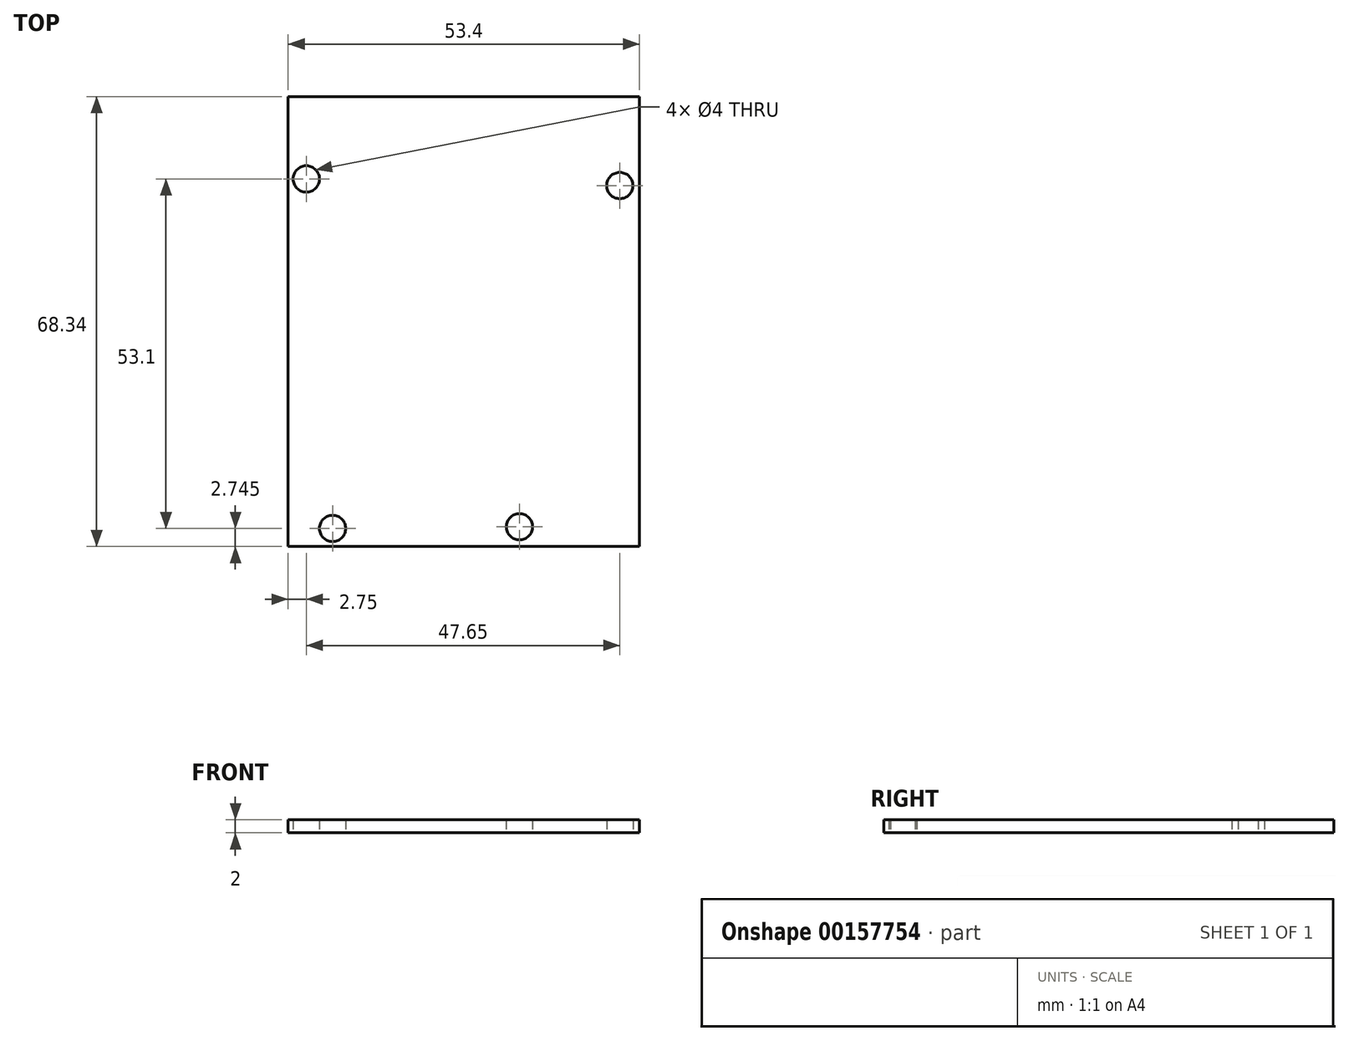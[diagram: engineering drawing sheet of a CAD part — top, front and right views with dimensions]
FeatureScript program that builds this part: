
annotation { "Feature Type Name" : "Feature", "Feature Type Description" : "" }
export const myFeature = defineFeature(function(context is Context, id is Id, definition is map)
    precondition{}
    {
        {
            var Q0;
            Q0=qCreatedBy(makeId("Top.planeOp"),FACE);
            var sketch = newSketch(context, id + "F0", { "sketchPlane" : qUnion([Q0])});
            skLineSegment(sketch, "E0.bottom", {"start": v(26.7, 34.17) * mm, "end": v(-26.7, 34.17) * mm});
            skLineSegment(sketch, "E0.top", {"start": v(26.7, -34.17) * mm, "end": v(-26.7, -34.17) * mm});
            skLineSegment(sketch, "E0.left", {"start": v(26.7, 34.17) * mm, "end": v(26.7, -34.17) * mm});
            skLineSegment(sketch, "E0.right", {"start": v(-26.7, 34.17) * mm, "end": v(-26.7, -34.17) * mm});
            skPoint(sketch, "E0.middle", {"position": v(0, 0) * mm});
            skLineSegment(sketch, "E1", {"start": v(-26.7, 34.17) * mm, "end": v(-26.7, 21.67) * mm});
            skLineSegment(sketch, "E2", {"start": v(-26.7, 21.67) * mm, "end": v(-23.95, 21.67) * mm});
            skCircle(sketch, "E3", {"center": v(-23.95, 21.67) * mm, "radius": 2 * mm});
            skLineSegment(sketch, "E4", {"start": v(26.7, 34.17) * mm, "end": v(26.7, 20.67) * mm});
            skLineSegment(sketch, "E5", {"start": v(26.7, 20.67) * mm, "end": v(23.7, 20.67) * mm});
            skCircle(sketch, "E6", {"center": v(23.7, 20.67) * mm, "radius": 2 * mm});
            skLineSegment(sketch, "E7", {"start": v(26.7, -34.17) * mm, "end": v(8.45, -34.17) * mm});
            skLineSegment(sketch, "E8", {"start": v(8.45, -34.17) * mm, "end": v(8.45, -31.17) * mm});
            skCircle(sketch, "E9", {"center": v(8.45, -31.17) * mm, "radius": 2 * mm});
            skLineSegment(sketch, "E10", {"start": v(-26.7, -34.17) * mm, "end": v(-19.95, -34.17) * mm});
            skLineSegment(sketch, "E11", {"start": v(-19.95, -34.17) * mm, "end": v(-19.95, -31.42) * mm});
            skCircle(sketch, "E12", {"center": v(-19.95, -31.42) * mm, "radius": 2 * mm});
            skSolve(sketch);
        }
        {
            var Q0;
            Q0=makeQuery(id+"F0.imprint","IMPRINT",FACE,{"disambiguationData":[TD([[makeQuery(id+"F0.imprint","IMPRINT",EDGE,{"derivedFrom":sQuery(id+"F0.wireOp",EDGE,"E0.bottom")}),1.0]])]});
            extrude(context, id + "F1", {"entities" : qUnion([Q0]), "depth" : 2 * mm});
        }
    });
